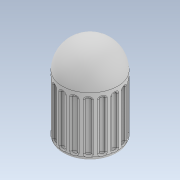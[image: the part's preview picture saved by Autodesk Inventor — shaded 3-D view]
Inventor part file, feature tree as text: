
AUTODESK INVENTOR PART (.ipt)
format: ipt  version: 2022 (Build 260153000, 153)  size: 1,265,664 bytes
history: native  units: in
note: dims shown in document units (in); Inventor stores cm internally (conversion verified against a paired STEP export)
features: sketch x4, other x4, fillet x3, revolve x2, pattern_circular x2, thread x1, plane x1, extrude x1, helix x1
ambient origin geometry x8: Origin, YZ Plane, XZ Plane, XY Plane, X Axis, Y Axis, Z Axis, Center Point
bodies: Solid9 (feature_tree)
feature tree (19):
  sketch  "Sketch3"  dims[d3=90.0deg d4=0.2331in d5=0.0in d15=0.3779in d26=0.0157in]
  revolve  "Revolution2"  [1 undecoded]
  other  "Work Axis1"
  other  "Work Point3"
  other  "Work Point4"
  thread  "Thread1"  [1 undecoded]
  fillet  "Fillet1"  Radius=0.0157in
  plane  "Work Plane1"
  extrude  "Extrusion2"  [1 undecoded]
  fillet  "Fillet3"  Radius=0.1969in
  pattern_circular  "Circular Pattern1"  Count=17 Angle=360.0deg
  fillet  "Fillet4"  Radius=0.0059in
  pattern_circular  "Circular Pattern2"  Count=17 Angle=360.0deg
  other  "Work Point5"
  revolve  "Revolution10"  [1 undecoded]
  helix  "Coil7"  [1 undecoded]
  sketch  "Sketch11"  dims[d34=0.3779in d48=-0.0197in d49=0.1969in d50=0.0in]
  sketch  "Sketch21"  dims[d51=0.0059in d52=6.6929in d53=360.0deg d55=0.0059in d56=6.6929in d57=360.0deg]
  sketch  "Sketch22"  dims[d67=0.3779in d85=0.3779in d103=0.3779in d121=0.3779in d132=0.3779in d133=0.0044in d134=0.0044in d137=0.0276in d139=0.3779in d141=0.0in d142=0.0276in d143=0.2882in d144=0.3937in d145=0.0in d146=0.0in d147=0.0in d148=0.0in d149=0.0in]
note: 5 required parameter values undecoded (feature->parameter linkage not recoverable at this tier; creation-order binding heuristic only, values carry confidence <= 0.55)